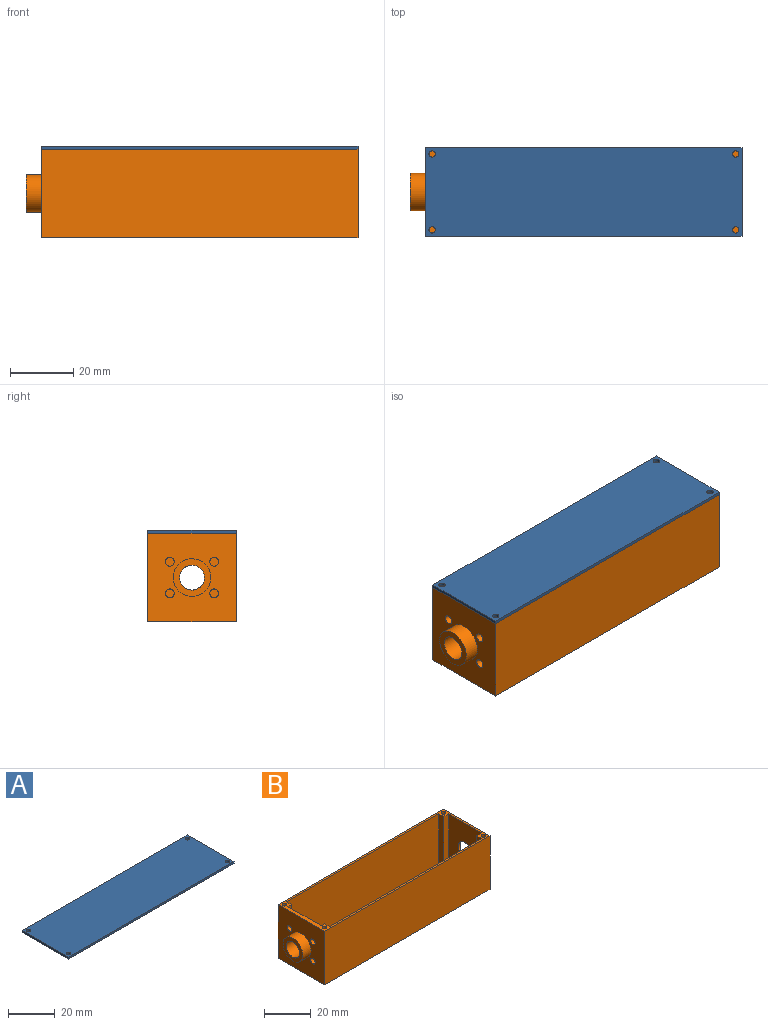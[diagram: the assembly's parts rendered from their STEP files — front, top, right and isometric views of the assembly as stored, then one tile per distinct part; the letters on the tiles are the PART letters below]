
ASSEMBLY  parts=2 mates=1
PART A: 23 faces, bbox 100x28x2 mm
  f0: plane 100x28mm, normal (0,0,1), area 2787.4mm2, adj f2,f3,f4,f5,f19,f20,f21,f22
  f1: plane 100x28mm, normal (0,0,-1), area 295.4mm2, adj f2,f3,f4,f5,f6,f7,f8,f9
  f2: plane 28x1mm, normal (-1,0,0), area 28mm2, adj f0,f1,f3,f5
  f3: plane 100x1mm, normal (0,-1,0), area 100mm2, adj f0,f1,f2,f4
  f4: plane 28x1mm, normal (1,0,0), area 28mm2, adj f0,f1,f3,f5
  f5: plane 100x1mm, normal (0,1,0), area 100mm2, adj f0,f1,f2,f4
  f6: plane 2x1mm, normal (0,-1,0), area 2mm2, adj f1,f7,f17,f18
  f7: plane 20x1mm, normal (-1,0,0), area 20mm2, adj f1,f6,f8,f18
  f8: plane 2x1mm, normal (0,1,0), area 2mm2, adj f1,f7,f9,f18
  f9: plane 3x1mm, normal (-1,0,0), area 3mm2, adj f1,f8,f10,f18
  f10: plane 92x1mm, normal (0,1,0), area 92mm2, adj f1,f9,f11,f18
  f11: plane 3x1mm, normal (1,0,0), area 3mm2, adj f1,f10,f12,f18
  f12: plane 3x1mm, normal (0,1,0), area 3mm2, adj f1,f11,f13,f18
  f13: plane 20x1mm, normal (1,0,0), area 20mm2, adj f1,f12,f14,f18
  f14: plane 3x1mm, normal (0,-1,0), area 3mm2, adj f1,f13,f15,f18
  f15: plane 3x1mm, normal (1,0,0), area 3mm2, adj f1,f14,f16,f18
  f16: plane 92x1mm, normal (0,-1,0), area 92mm2, adj f1,f15,f17,f18
  f17: plane 3x1mm, normal (-1,0,0), area 3mm2, adj f1,f6,f16,f18
  f18: plane 97x26mm, normal (0,0,-1), area 2492mm2, adj f6,f7,f8,f9,f10,f11,f12,f13
  f19: cylinder r=1mm len=2mm, axis (0,0,-1), area 6.3mm2, adj f0,f1
  f20: cylinder r=1mm len=2mm, axis (0,0,-1), area 6.3mm2, adj f0,f1
  f21: cylinder r=1mm len=2mm, axis (0,0,-1), area 6.3mm2, adj f0,f1
  f22: cylinder r=1mm len=2mm, axis (0,0,-1), area 6.3mm2, adj f0,f1
PART B: 37 faces, bbox 105x28x28 mm
  f0: plane 100x28mm, normal (0,0,1), area 295.4mm2, adj f1,f2,f3,f4,f5,f7,f8,f9
  f1: plane 28x28mm, normal (-1,0,0), area 648.1mm2, adj f0,f3,f5,f6,f19,f20,f21,f22
  f2: plane 27x20mm, normal (1,0,0), area 404.1mm2, adj f0,f7,f17,f18,f19,f20,f21,f22
  f3: plane 100x28mm, normal (0,-1,0), area 2800mm2, adj f0,f1,f4,f6
  f4: plane 28x28mm, normal (1,0,0), area 733.7mm2, adj f0,f3,f5,f6,f36
  f5: plane 100x28mm, normal (0,1,0), area 2800mm2, adj f0,f1,f4,f6
  f6: plane 100x28mm, normal (0,0,-1), area 2800mm2, adj f1,f3,f4,f5
  f7: plane 27x2mm, normal (0,-1,0), area 54mm2, adj f0,f2,f8,f18
  f8: plane 27x3mm, normal (1,0,0), area 81mm2, adj f0,f7,f9,f18
  f9: plane 92x27mm, normal (0,-1,0), area 2484mm2, adj f0,f8,f10,f18
  f10: plane 27x3mm, normal (-1,0,0), area 81mm2, adj f0,f9,f11,f18
  f11: plane 27x3mm, normal (0,-1,0), area 81mm2, adj f0,f10,f12,f18
  f12: plane 27x20mm, normal (-1,0,0), area 489.7mm2, adj f0,f11,f13,f18,f36
  f13: plane 27x3mm, normal (0,1,0), area 81mm2, adj f0,f12,f14,f18
  f14: plane 27x3mm, normal (-1,0,0), area 81mm2, adj f0,f13,f15,f18
  f15: plane 92x27mm, normal (0,1,0), area 2484mm2, adj f0,f14,f16,f18
  f16: plane 27x3mm, normal (1,0,0), area 81mm2, adj f0,f15,f17,f18
  f17: plane 27x2mm, normal (0,1,0), area 54mm2, adj f0,f2,f16,f18
  f18: plane 97x26mm, normal (0,0,1), area 2492mm2, adj f2,f7,f8,f9,f10,f11,f12,f13
  f19: cylinder r=1.4mm len=2.8mm, axis (-1,0,0), area 17.6mm2, adj f1,f2
  f20: cylinder r=1.4mm len=2.8mm, axis (-1,0,0), area 17.6mm2, adj f1,f2
  f21: cylinder r=1.4mm len=2.8mm, axis (-1,0,0), area 17.6mm2, adj f1,f2
  f22: cylinder r=1.4mm len=2.8mm, axis (-1,0,0), area 17.6mm2, adj f1,f2
  f23: cylinder r=3.95mm len=12mm, axis (-1,0,0), area 297.8mm2, adj f25,f27
  f24: cylinder r=5.95mm len=11.9mm, axis (1,0,0), area 186.9mm2, adj f1,f25
  f25: plane 11.9x11.9mm, normal (-1,0,0), area 62.2mm2, adj f23,f24
  f26: cylinder r=5.95mm len=11.9mm, axis (-1,0,0), area 186.9mm2, adj f2,f27
  f27: plane 11.9x11.9mm, normal (1,0,0), area 62.2mm2, adj f23,f26
  f28: cylinder r=1mm len=4mm, axis (0,0,1), area 25.1mm2, adj f0,f29
  f29: plane 2x2mm, normal (0,0,1), area 3.1mm2, adj f28
  f30: cylinder r=1mm len=4mm, axis (0,0,1), area 25.1mm2, adj f0,f31
  f31: plane 2x2mm, normal (0,0,1), area 3.1mm2, adj f30
  f32: cylinder r=1mm len=4mm, axis (0,0,1), area 25.1mm2, adj f0,f33
  f33: plane 2x2mm, normal (0,0,1), area 3.1mm2, adj f32
  f34: cylinder r=1mm len=4mm, axis (0,0,1), area 25.1mm2, adj f0,f35
  f35: plane 2x2mm, normal (0,0,1), area 3.1mm2, adj f34
  f36: cylinder r=4mm len=8mm, axis (1,0,0), area 25.1mm2, adj f4,f12
PLACE A t=(64.73,11.78,18.56)mm
PLACE B t=(64.73,11.78,-9.44)mm
MATE fastened B.f0 <-> A.f1  axis (0,0,1) through (64.73,11.78,18.56)mm
